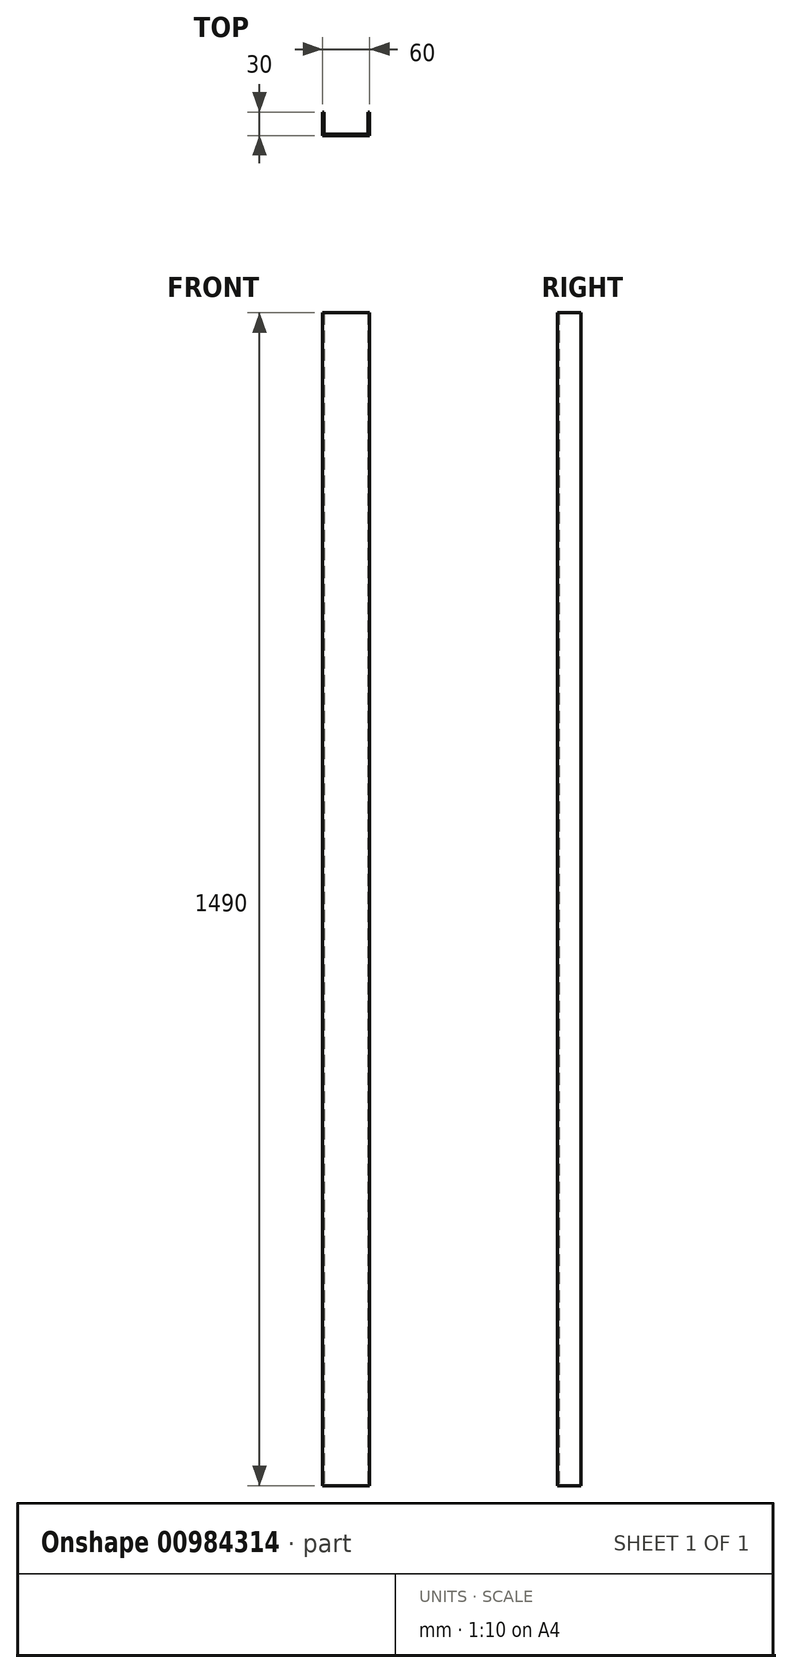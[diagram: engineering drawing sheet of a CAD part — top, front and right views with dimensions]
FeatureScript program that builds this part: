
annotation { "Feature Type Name" : "Feature", "Feature Type Description" : "" }
export const myFeature = defineFeature(function(context is Context, id is Id, definition is map)
    precondition{}
    {
        {
            var Q0;
            Q0=qCreatedBy(makeId("Top.planeOp"),FACE);
            var sketch = newSketch(context, id + "F0", { "sketchPlane" : qUnion([Q0])});
            skLineSegment(sketch, "E0", {"start": v(0, 0) * mm, "end": v(60, 0) * mm});
            skLineSegment(sketch, "E1", {"start": v(60, 0) * mm, "end": v(60, 30) * mm});
            skLineSegment(sketch, "E2", {"start": v(0, 0) * mm, "end": v(0, 30) * mm});
            skLineSegment(sketch, "E3", {"start": v(0, 30) * mm, "end": v(0, 30) * mm});
            skLineSegment(sketch, "E4", {"start": v(60, 30) * mm, "end": v(60, 30) * mm});
            skLineSegment(sketch, "E5.0", {"start": v(58, 2) * mm, "end": v(58, 30) * mm});
            skLineSegment(sketch, "E5.1", {"start": v(2, 2) * mm, "end": v(58, 2) * mm});
            skLineSegment(sketch, "E5.2", {"start": v(2, 2) * mm, "end": v(2, 30) * mm});
            skLineSegment(sketch, "E6", {"start": v(0, 30) * mm, "end": v(2, 30) * mm});
            skLineSegment(sketch, "E7", {"start": v(58, 30) * mm, "end": v(60, 30) * mm});
            skSolve(sketch);
        }
        {
            var Q0;
            Q0=makeQuery(id+"F0.imprint","IMPRINT",FACE,{"disambiguationData":[TD([[makeQuery(id+"F0.imprint","IMPRINT",EDGE,{"derivedFrom":sQuery(id+"F0.wireOp",EDGE,"E0")}),1.0]])]});
            extrude(context, id + "F1", {"entities" : qUnion([Q0]), "depth" : (1500 - 10) * mm, "offsetDistance" : 25 * mm});
        }
    });
